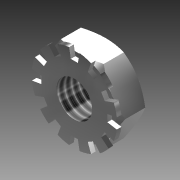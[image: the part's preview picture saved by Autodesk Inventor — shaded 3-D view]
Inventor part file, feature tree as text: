
AUTODESK INVENTOR PART (.ipt)
format: ipt  version: 2015 (Build 190159000, 159)  size: 212,992 bytes
history: native  units: mm (DEFAULTED — no unit token found)
features: sketch x5, extrude x4, revolve x1, plane x1, mirror x1, thread x1, pattern_circular x1
ambient origin geometry x5: Origin, YZ Plane, XZ Plane, XY Plane, Center Point
bodies: Solid1 (feature_tree)
feature tree (14):
  extrude  "Extrusion2"  Depth=8.73252mm
  revolve  "Revolution1"  Angle=90.0deg
  plane  "Work Plane1"
  mirror  "Mirror1"
  extrude  "Extrusion3"  Depth=25.4mm TaperAngle=0.0deg
  thread  "Thread1"  [1 undecoded]
  extrude  "Extrusion5"  TaperAngle=0.0deg  [1 undecoded]
  extrude  "Extrusion6"  Depth=17.453293mm
  pattern_circular  "Circular Pattern1"  [2 undecoded]
  sketch  "Sketch2"  dims[d4=0.0mm d6=8.73252mm]
  sketch  "Sketch4"  dims[d7=30.0deg d8=90.0deg]
  sketch  "Sketch5"  dims[d11=6.35mm d12=0.0mm d13=25.4mm d14=0.0mm d18=10.042398mm]
  sketch  "Sketch7"  dims[d19=0.545548mm d20=0.0mm]
  sketch  "Sketch8"  dims[d21=17.453293mm d22=17.453293mm d23=3.88112mm d24=0.83312mm d25=0.545548mm d26=0.0mm d27=120.0mm d29=360.0deg]
note: 4 required parameter values undecoded (feature->parameter linkage not recoverable at this tier; creation-order binding heuristic only, values carry confidence <= 0.55)
